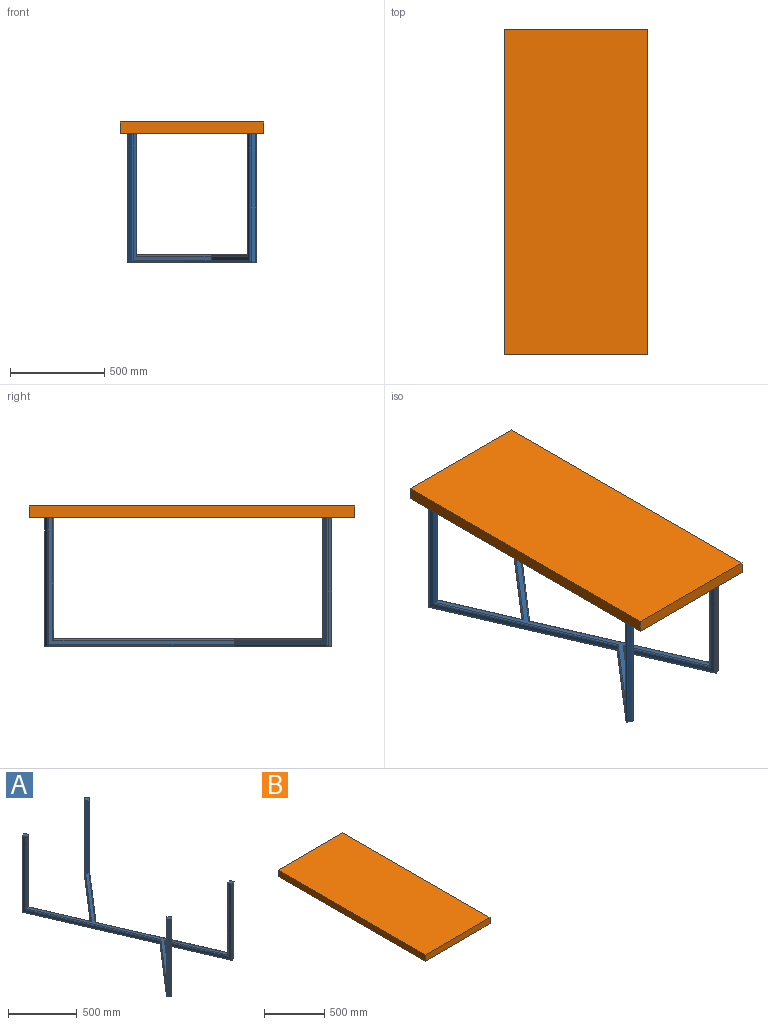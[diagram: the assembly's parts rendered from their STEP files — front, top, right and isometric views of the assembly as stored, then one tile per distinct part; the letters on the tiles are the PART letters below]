
ASSEMBLY  parts=2 mates=1
PART A: 54 faces, bbox 688.7x1526.9x679.5 mm
  f0: cylinder r=6.35mm len=996.06mm, axis (-0.4,0.92,0), area 10743.3mm2, adj f15,f23,f24,f42
  f1: cylinder r=6.35mm len=966.9mm, axis (-0.4,0.92,0), area 10409.3mm2, adj f18,f24,f25,f43
  f2: plane 673.1x473.6mm, normal (0.92,0.4,0), area 29551mm2, adj f6,f10,f11,f16,f17,f48
  f3: cylinder r=6.35mm len=491.25mm, axis (-0.4,0.92,0), area 5221.1mm2, adj f5,f15,f21,f29
  f4: cylinder r=6.35mm len=966.9mm, axis (-0.4,0.92,0), area 10409.3mm2, adj f8,f18,f20,f31
  f5: plane 673.1x473.6mm, normal (-0.92,-0.4,0), area 29551mm2, adj f3,f7,f19,f21,f27,f33
  f6: plane 46.08x46.08mm, normal (0,0,1), area 1417mm2, adj f2,f8,f9,f10,f11,f12,f13,f20
  f7: plane 46.08x46.08mm, normal (0,0,1), area 1417mm2, adj f5,f21,f22,f23,f24,f25,f26,f27
  f8: cylinder r=6.35mm len=647.7mm, axis (0,0,1), area 6420.2mm2, adj f4,f6,f9,f20
  f9: plane 641.35x23.33mm, normal (0.4,-0.92,0), area 16290.3mm2, adj f6,f8,f10,f18
  f10: cylinder r=6.35mm len=647.7mm, axis (0,0,1), area 6420.2mm2, adj f2,f6,f9,f17
  f11: cylinder r=6.35mm len=679.45mm, axis (0,0,1), area 6754.2mm2, adj f2,f6,f12,f16
  f12: plane 679.45x23.33mm, normal (-0.4,0.92,0), area 17258mm2, adj f6,f11,f13,f15
  f13: cylinder r=6.35mm len=679.45mm, axis (0,0,1), area 6754.2mm2, adj f6,f12,f14,f20
  f14: cylinder r=6.35mm len=996.06mm, axis (-0.4,0.92,0), area 10743.3mm2, adj f13,f15,f20,f30
  f15: plane 1518.63x679.14mm, normal (0,0,-1), area 74872.6mm2, adj f0,f3,f12,f14,f16,f22,f29,f30
  f16: cylinder r=6.35mm len=491.25mm, axis (-0.4,0.92,0), area 5221.1mm2, adj f2,f11,f15,f45
  f17: cylinder r=6.35mm len=462.09mm, axis (-0.4,0.92,0), area 4887.1mm2, adj f2,f10,f18,f44
  f18: plane 1461.01x643.24mm, normal (0,0,1), area 71001.6mm2, adj f1,f4,f9,f17,f19,f26,f31,f32
  f19: cylinder r=6.35mm len=462.09mm, axis (-0.4,0.92,0), area 4887.1mm2, adj f5,f18,f27,f32
  f20: plane 984.06x673.1mm, normal (-0.92,-0.4,0), area 43669.7mm2, adj f4,f6,f8,f13,f14,f37
  f21: cylinder r=6.35mm len=679.45mm, axis (0,0,-1), area 6754.2mm2, adj f3,f5,f7,f22
  f22: plane 679.45x23.33mm, normal (0.4,-0.92,0), area 17258mm2, adj f7,f15,f21,f23
  f23: cylinder r=6.35mm len=679.45mm, axis (0,0,-1), area 6754.2mm2, adj f0,f7,f22,f24
  f24: plane 984.06x673.1mm, normal (0.92,0.4,0), area 43669.7mm2, adj f0,f1,f7,f23,f25,f52
  f25: cylinder r=6.35mm len=647.7mm, axis (0,0,-1), area 6420.2mm2, adj f1,f7,f24,f26
  f26: plane 641.35x23.33mm, normal (-0.4,0.92,0), area 16290.3mm2, adj f7,f18,f25,f27
  f27: cylinder r=6.35mm len=647.7mm, axis (0,0,-1), area 6420.2mm2, adj f5,f7,f19,f26
  f28: plane 48.53x48.53mm, normal (0,0,1), area 1417mm2, adj f33,f34,f35,f36,f37,f38,f39,f40
  f29: cylinder r=6.35mm len=493.08mm, axis (0.65,0.76,0), area 6361.9mm2, adj f3,f15,f33,f40
  f30: cylinder r=6.35mm len=502.37mm, axis (0.65,0.76,0), area 6523.4mm2, adj f14,f15,f37,f38
  f31: cylinder r=6.35mm len=478.36mm, axis (0.65,0.76,0), area 6189.4mm2, adj f4,f18,f36,f37
  f32: cylinder r=6.35mm len=469.07mm, axis (0.65,0.76,0), area 6027.9mm2, adj f18,f19,f33,f34
  f33: plane 673.1x476.47mm, normal (0.76,-0.65,0), area 32455.8mm2, adj f5,f28,f29,f32,f34,f40
  f34: cylinder r=6.35mm len=647.7mm, axis (0,0,-1), area 6420.2mm2, adj f28,f32,f33,f35
  f35: plane 641.35x19.21mm, normal (0.65,0.76,0), area 16290.3mm2, adj f18,f28,f34,f36
  f36: cylinder r=6.35mm len=647.7mm, axis (0,0,-1), area 6420.2mm2, adj f28,f31,f35,f37
  f37: plane 673.1x490.4mm, normal (-0.76,0.65,0), area 32923.9mm2, adj f20,f28,f30,f31,f36,f38
  f38: cylinder r=6.35mm len=679.45mm, axis (0,0,-1), area 6754.2mm2, adj f28,f30,f37,f39
  f39: plane 679.45x19.21mm, normal (-0.65,-0.76,0), area 17258mm2, adj f15,f28,f38,f40
  f40: cylinder r=6.35mm len=679.45mm, axis (0,0,-1), area 6754.2mm2, adj f28,f29,f33,f39
  f41: plane 48.53x48.53mm, normal (0,0,1), area 1417mm2, adj f46,f47,f48,f49,f50,f51,f52,f53
  f42: cylinder r=6.35mm len=502.37mm, axis (-0.65,-0.76,0), area 6523.4mm2, adj f0,f15,f52,f53
  f43: cylinder r=6.35mm len=478.36mm, axis (-0.65,-0.76,0), area 6189.4mm2, adj f1,f18,f51,f52
  f44: cylinder r=6.35mm len=469.07mm, axis (-0.65,-0.76,0), area 6027.9mm2, adj f17,f18,f48,f49
  f45: cylinder r=6.35mm len=493.08mm, axis (-0.65,-0.76,0), area 6361.9mm2, adj f15,f16,f47,f48
  f46: plane 679.45x19.21mm, normal (0.65,0.76,0), area 17258mm2, adj f15,f41,f47,f53
  f47: cylinder r=6.35mm len=679.45mm, axis (0,0,-1), area 6754.2mm2, adj f41,f45,f46,f48
  f48: plane 673.1x476.47mm, normal (-0.76,0.65,0), area 32455.8mm2, adj f2,f41,f44,f45,f47,f49
  f49: cylinder r=6.35mm len=647.7mm, axis (0,0,-1), area 6420.2mm2, adj f41,f44,f48,f50
  f50: plane 641.35x19.21mm, normal (-0.65,-0.76,0), area 16290.3mm2, adj f18,f41,f49,f51
  f51: cylinder r=6.35mm len=647.7mm, axis (0,0,-1), area 6420.2mm2, adj f41,f43,f50,f52
  f52: plane 673.1x490.4mm, normal (0.76,-0.65,0), area 32923.9mm2, adj f24,f41,f42,f43,f51,f53
  f53: cylinder r=6.35mm len=679.45mm, axis (0,0,-1), area 6754.2mm2, adj f41,f42,f46,f52
PART B: 6 faces, bbox 762x1727.2x63.5 mm
  f0: plane 1727.2x63.5mm, normal (-1,0,0), area 109677.2mm2, adj f1,f3,f4,f5
  f1: plane 762x63.5mm, normal (0,-1,0), area 48387mm2, adj f0,f2,f4,f5
  f2: plane 1727.2x63.5mm, normal (1,0,0), area 109677.2mm2, adj f1,f3,f4,f5
  f3: plane 762x63.5mm, normal (0,1,0), area 48387mm2, adj f0,f2,f4,f5
  f4: plane 1727.2x762mm, normal (0,0,1), area 1316126.4mm2, adj f0,f1,f2,f3
  f5: plane 1727.2x762mm, normal (0,0,-1), area 1316126.4mm2, adj f0,f1,f2,f3
PLACE A t=(260.65,324.81,-39.91)mm fixed
PLACE B t=(118.56,305.81,620.49)mm
MATE planar A.f28 <-> B.f5  axis (0,0,1) through (-198.8,-411.2,620.49)mm
